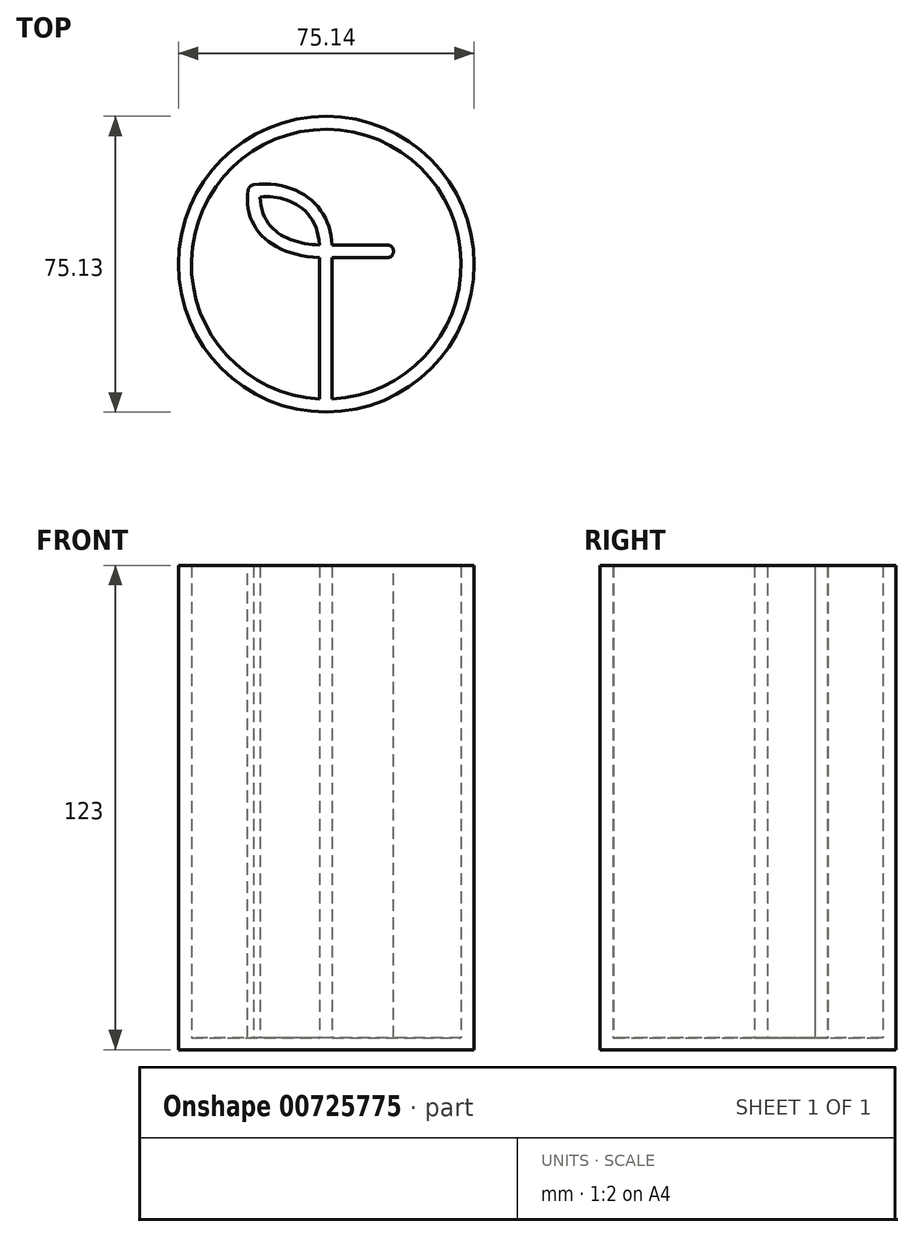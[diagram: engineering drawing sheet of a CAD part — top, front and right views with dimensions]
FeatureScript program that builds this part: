
annotation { "Feature Type Name" : "Feature", "Feature Type Description" : "" }
export const myFeature = defineFeature(function(context is Context, id is Id, definition is map)
    precondition{}
    {
        {
            var Q0;
            Q0=qCreatedBy(makeId("Top.planeOp"),FACE);
            var sketch = newSketch(context, id + "F0", { "sketchPlane" : qUnion([Q0])});
            skCircle(sketch, "E0", {"center": v(-84.92, -13.22) * mm, "radius": 25.05 * mm});
            skPoint(sketch, "E0.first.point", {"position": v(-109.96, -13.18) * mm});
            skPoint(sketch, "E0.second.point", {"position": v(-65.08, 2.07) * mm});
            skPoint(sketch, "E0.third.point", {"position": v(-84.87, -38.27) * mm});
            skCircle(sketch, "E1.0", {"center": v(-84.92, -13.22) * mm, "radius": 22.85 * mm});
            skLineSegment(sketch, "E2", {"start": v(-74.54, -12.1) * mm, "end": v(-83.98, -12.1) * mm});
            skLineSegment(sketch, "E3", {"start": v(-83.98, -12.1) * mm, "end": v(-83.98, -38.25) * mm});
            skLineSegment(sketch, "E4", {"start": v(-86.08, -38.24) * mm, "end": v(-86.08, -12.1) * mm});
            skLineSegment(sketch, "E5", {"start": v(-74.54, -9.97) * mm, "end": v(-83.98, -9.97) * mm});
            skFitSpline(sketch, "E6", {"points": [v(-83.98, -9.97) * mm, v(-97.28, 0.23) * mm], "startDerivative": vector(-0.3, 18.87) * mm, "endDerivative": vector(-23.63, -2.85) * mm});
            skFitSpline(sketch, "E7", {"points": [v(-86.08, -12.1) * mm, v(-98.16, -0.7) * mm], "startDerivative": vector(-24.73, 0.93) * mm, "endDerivative": vector(3, 18.54) * mm});
            skFitSpline(sketch, "E8", {"points": [v(-74.54, -9.97) * mm, v(-74.54, -12.1) * mm], "startDerivative": vector(3.97, 0) * mm, "endDerivative": vector(-3.97, 0) * mm});
            skFitSpline(sketch, "E9", {"points": [v(-98.16, -0.7) * mm, v(-97.28, 0.23) * mm], "startDerivative": vector(0.28, 1.73) * mm, "endDerivative": vector(1.34, 0.35) * mm});
            skFitSpline(sketch, "E10", {"points": [v(-86.08, -9.97) * mm, v(-96.12, -1.85) * mm], "startDerivative": vector(-0.94, 19.47) * mm, "endDerivative": vector(-12.47, -1.36) * mm});
            skFitSpline(sketch, "E11", {"points": [v(-96.12, -1.85) * mm, v(-86.08, -9.97) * mm], "startDerivative": vector(0.58, -18.07) * mm, "endDerivative": vector(14.35, -0.58) * mm});
            skSolve(sketch);
        }
        {
            var Q0;
            Q0 = qSketchRegion(id + "F0", true);
            var Q1;
            {var subQ6=sQuery(id+"F0.wireOp",EDGE,"E2");Q1=makeQuery(id+"F0.imprint","IMPRINT",FACE,{"disambiguationData":[TD([[makeQuery(id+"F0.imprint","IMPRINT",EDGE,{"derivedFrom":subQ6}),-1.0]])]});}
            extrude(context, id + "F1", {"entities" : qUnion([Q0, Q1]), "depth" : 80 * mm, "offsetDistance" : 25 * mm});
        }
        {
            var Q0;
            Q0=makeQuery(id+"F1.opExtrude","CAP_FACE",FACE,{"disambiguationData":[OSD([sQuery(id+"F0.wireOp",EDGE,"E0"),sQuery(id+"F0.wireOp",EDGE,"E1.0"),sQuery(id+"F0.wireOp",EDGE,"E2"),sQuery(id+"F0.wireOp",EDGE,"E3"),sQuery(id+"F0.wireOp",EDGE,"E4"),sQuery(id+"F0.wireOp",EDGE,"E5"),sQuery(id+"F0.wireOp",EDGE,"E6"),sQuery(id+"F0.wireOp",EDGE,"E7"),sQuery(id+"F0.wireOp",EDGE,"E8"),sQuery(id+"F0.wireOp",EDGE,"E9"),sQuery(id+"F0.wireOp",EDGE,"E10"),sQuery(id+"F0.wireOp",EDGE,"E11")])],"isStart":true});
            var sketch = newSketch(context, id + "F2", { "sketchPlane" : qUnion([Q0])});
            skCircle(sketch, "E12.0", {"center": v(-84.92, 13.22) * mm, "radius": 25.05 * mm});
            skSolve(sketch);
        }
        {
            var Q0;
            Q0 = qSketchRegion(id + "F2", true);
            extrude(context, id + "F3", {"entities" : qUnion([Q0]), "operationType" : NewBodyOperationType.ADD, "depth" : 2 * mm, "offsetDistance" : 25 * mm});
        }
        {
            var Q0;
            Q0=makeQuery(id+"F1.opExtrude","SWEPT_BODY",BODY,{"disambiguationData":[OSD([sQuery(id+"F0.wireOp",EDGE,"E0"),sQuery(id+"F0.wireOp",EDGE,"E1.0"),sQuery(id+"F0.wireOp",EDGE,"E2"),sQuery(id+"F0.wireOp",EDGE,"E3"),sQuery(id+"F0.wireOp",EDGE,"E4"),sQuery(id+"F0.wireOp",EDGE,"E5"),sQuery(id+"F0.wireOp",EDGE,"E6"),sQuery(id+"F0.wireOp",EDGE,"E7"),sQuery(id+"F0.wireOp",EDGE,"E8"),sQuery(id+"F0.wireOp",EDGE,"E9"),sQuery(id+"F0.wireOp",EDGE,"E10"),sQuery(id+"F0.wireOp",EDGE,"E11")])]});
            var Q1;
            Q1=makeQuery(id+"F1.opExtrude","CAP_VERTEX",VERTEX,{"disambiguationData":[OSD([sQuery(id+"F0.wireOp",EDGE,"E2"),sQuery(id+"F0.wireOp",EDGE,"E3")])],"isStart":false});
            transform(context, id + "F4", {"entities" : qUnion([Q0]), "transformType" : TransformType.SCALE_UNIFORMLY, "scale" : 1.5, "scalePoint" : qUnion([Q1]), "makeCopy" : false});
        }
    });
